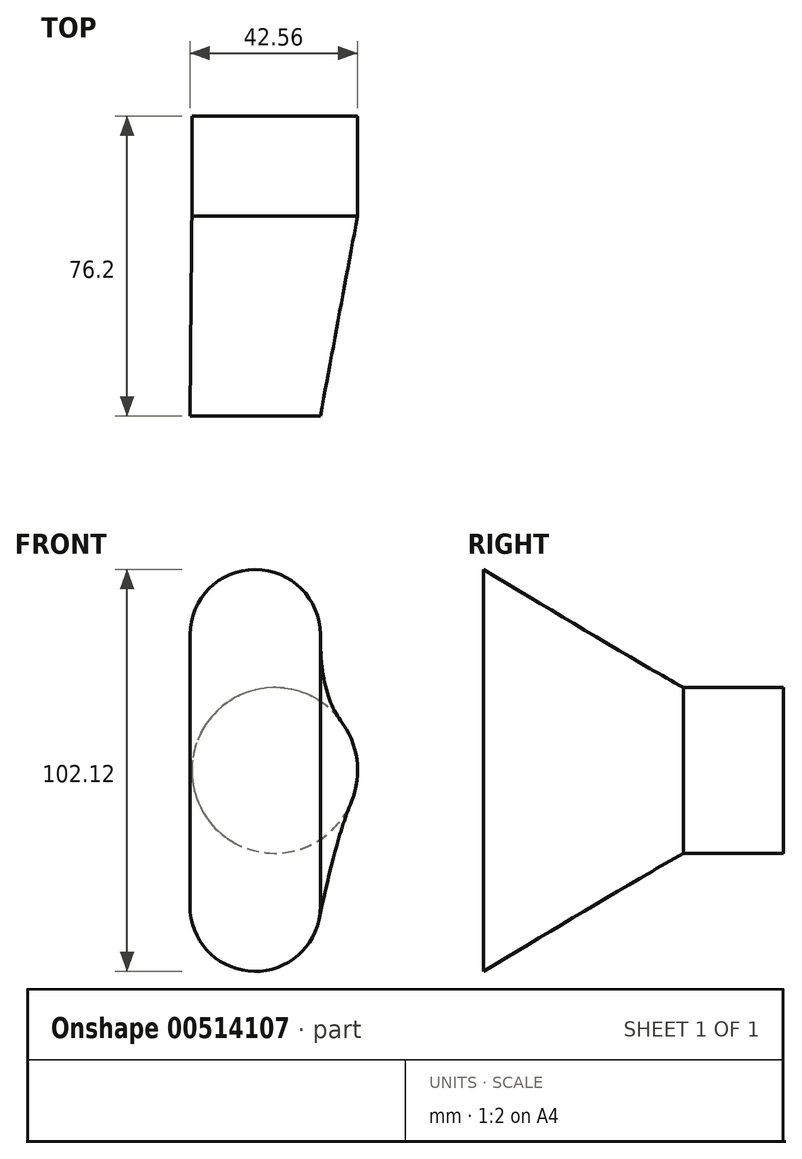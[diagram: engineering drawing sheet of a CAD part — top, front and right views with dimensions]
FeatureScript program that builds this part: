
annotation { "Feature Type Name" : "Feature", "Feature Type Description" : "" }
export const myFeature = defineFeature(function(context is Context, id is Id, definition is map)
    precondition{}
    {
        {
            var Q0;
            Q0=qCreatedBy(makeId("Front.planeOp"),FACE);
            var sketch = newSketch(context, id + "F0", { "sketchPlane" : qUnion([Q0])});
            skCircle(sketch, "E0", {"center": v(0, 0) * mm, "radius": 21.05 * mm});
            skSolve(sketch);
        }
        {
            var Q0;
            Q0=makeQuery(id+"F0.imprint","IMPRINT",FACE,{"disambiguationData":[TD([[makeQuery(id+"F0.imprint","IMPRINT",EDGE,{"derivedFrom":sQuery(id+"F0.wireOp",EDGE,"E0")}),1.0]])]});
            extrude(context, id + "F1", {"entities" : qUnion([Q0]), "depth" : 25.4 * mm, "offsetDistance" : 25.4 * mm});
        }
        {
            var Q0;
            Q0=makeQuery(id+"F1.opExtrude","CAP_FACE",FACE,{"disambiguationData":[OSD([sQuery(id+"F0.wireOp",EDGE,"E0")])],"isStart":false});
            var sketch = newSketch(context, id + "F2", { "sketchPlane" : qUnion([Q0])});
            skCircle(sketch, "E1.0", {"center": v(0, 0) * mm, "radius": 21.05 * mm});
            skPoint(sketch, "E2", {"position": v(-13.7, 15.98) * mm});
            skPoint(sketch, "E3", {"position": v(17.06, 12.32) * mm});
            skPoint(sketch, "E4", {"position": v(14.78, -14.99) * mm});
            skPoint(sketch, "E5", {"position": v(-14.78, -14.99) * mm});
            skSolve(sketch);
        }
        {
            var Q0;
            Q0=qCreatedBy(makeId("Front.planeOp"),FACE);
            cPlane(context, id + "F3", {"entities" : qUnion([Q0]), "cplaneType" : CPlaneType.OFFSET, "offset" : 76.2 * mm, "width" : 152.4 * mm, "height" : 152.4 * mm});
        }
        {
            var Q0;
            Q0=qCreatedBy(id+"F3.planeOp",FACE);
            var sketch = newSketch(context, id + "F4", { "sketchPlane" : qUnion([Q0])});
            skLineSegment(sketch, "E6.bottom", {"start": v(-21.5, -34.5) * mm, "end": v(11.6, -34.5) * mm, "construction": true});
            skLineSegment(sketch, "E6.top", {"start": v(-21.5, 34.5) * mm, "end": v(11.6, 34.5) * mm, "construction": true});
            skLineSegment(sketch, "E6.left", {"start": v(-21.5, -34.5) * mm, "end": v(-21.5, 34.5) * mm});
            skLineSegment(sketch, "E6.right", {"start": v(11.6, -34.5) * mm, "end": v(11.6, 34.5) * mm});
            skPoint(sketch, "E6.middle", {"position": v(-4.95, 0) * mm});
            skArc(sketch, "E7", {"start": v(11.6, 34.5) * mm, "mid": v(-4.95, 51.06) * mm, "end": v(-21.5, 34.5) * mm});
            skArc(sketch, "E8", {"start": v(-21.5, -34.5) * mm, "mid": v(-4.95, -51.06) * mm, "end": v(11.6, -34.5) * mm});
            skLineSegment(sketch, "E9", {"start": v(-4.95, 51.06) * mm, "end": v(-4.95, -51.06) * mm, "construction": true});
            skSolve(sketch);
        }
        {
            var Q0;
            Q0=makeQuery(id+"F4.imprint","IMPRINT",FACE,{"disambiguationData":[TD([[makeQuery(id+"F4.imprint","IMPRINT",EDGE,{"derivedFrom":sQuery(id+"F4.wireOp",EDGE,"E6.left")}),-1.0]])]});
            var Q1;
            Q1 = qSketchRegion(id + "F2", true);
            loft(context, id + "F5", {"sheetProfilesArray" : [{ "sheetProfileEntities" : qUnion([Q0]) }, { "sheetProfileEntities" : qUnion([Q1]) }]});
        }
    });
